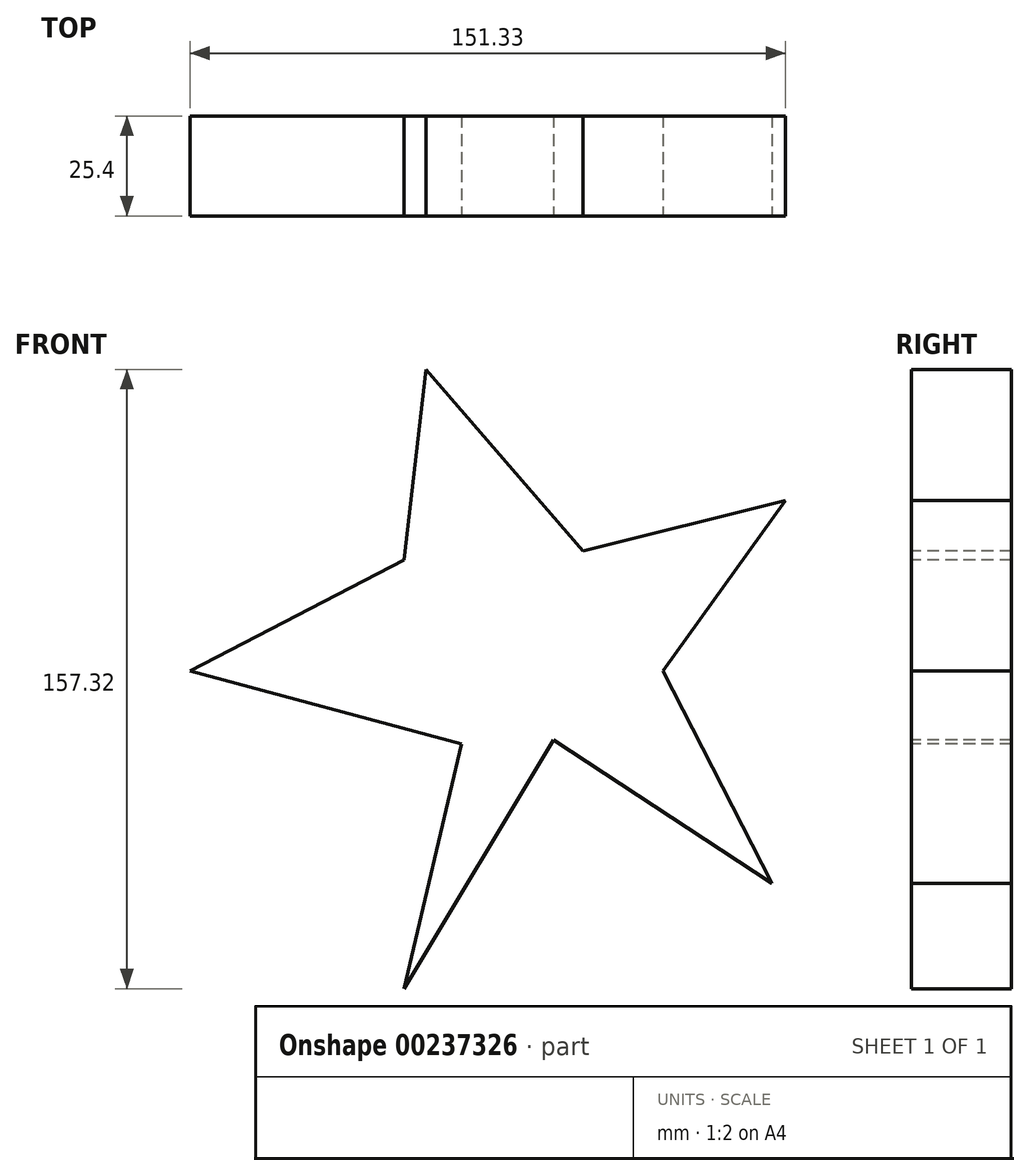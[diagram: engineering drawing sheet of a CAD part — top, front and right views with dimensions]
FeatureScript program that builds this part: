
annotation { "Feature Type Name" : "Feature", "Feature Type Description" : "" }
export const myFeature = defineFeature(function(context is Context, id is Id, definition is map)
    precondition{}
    {
        {
            var Q0;
            Q0=qCreatedBy(makeId("Front.planeOp"),FACE);
            var sketch = newSketch(context, id + "F0", { "sketchPlane" : qUnion([Q0])});
            skPoint(sketch, "E0.0.midPoint", {"position": v(66.91, -2.36) * mm});
            skLineSegment(sketch, "E1", {"start": v(-82.7, 2.91) * mm, "end": v(-13.76, -15.55) * mm});
            skLineSegment(sketch, "E2", {"start": v(-13.76, -15.55) * mm, "end": v(-28.33, -77.76) * mm});
            skLineSegment(sketch, "E3", {"start": v(-28.33, -77.76) * mm, "end": v(9.61, -14.6) * mm});
            skLineSegment(sketch, "E4", {"start": v(9.61, -14.6) * mm, "end": v(65.2, -50.97) * mm});
            skLineSegment(sketch, "E5", {"start": v(65.2, -50.97) * mm, "end": v(37.5, 2.91) * mm});
            skLineSegment(sketch, "E6", {"start": v(37.5, 2.91) * mm, "end": v(68.62, 46.26) * mm});
            skLineSegment(sketch, "E7", {"start": v(68.62, 46.26) * mm, "end": v(17.15, 33.46) * mm});
            skLineSegment(sketch, "E8", {"start": v(17.15, 33.46) * mm, "end": v(-22.79, 79.56) * mm});
            skLineSegment(sketch, "E9", {"start": v(-22.79, 79.56) * mm, "end": v(-28.33, 31.2) * mm});
            skLineSegment(sketch, "E10", {"start": v(-28.33, 31.2) * mm, "end": v(-82.7, 2.91) * mm});
            skSolve(sketch);
        }
        {
            var Q0;
            Q0 = qSketchRegion(id + "F0", true);
            extrude(context, id + "F1", {"entities" : qUnion([Q0]), "oppositeDirection" : true, "depth" : 25.4 * mm});
        }
    });
